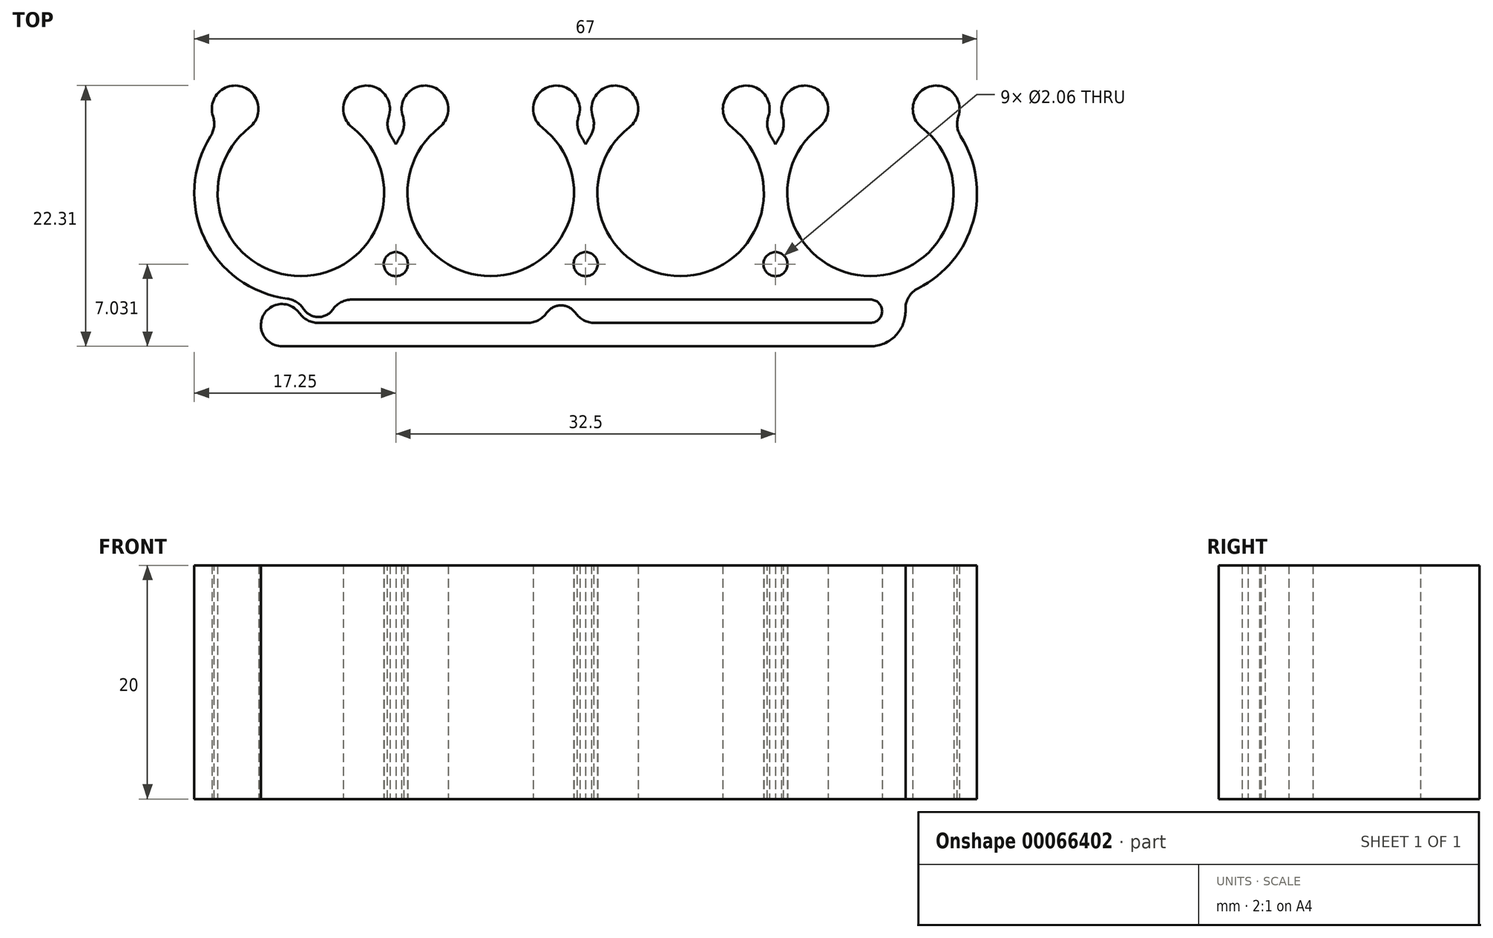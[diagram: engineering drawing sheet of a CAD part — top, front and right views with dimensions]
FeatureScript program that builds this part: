
annotation { "Feature Type Name" : "Feature", "Feature Type Description" : "" }
export const myFeature = defineFeature(function(context is Context, id is Id, definition is map)
    precondition{}
    {
        {
            assignVariable(context, id + "F0", {"name" : "Wall", "anyValue" : 2});
        }
        {
            var Q0;
            Q0=qCreatedBy(makeId("Top.planeOp"),FACE);
            var sketch = newSketch(context, id + "F1", { "sketchPlane" : qUnion([Q0])});
            skCircle(sketch, "E0", {"center": v(-24.38, 9.13) * mm, "radius": 7.12 * mm});
            skCircle(sketch, "E1", {"center": v(-8.12, 9.13) * mm, "radius": 7.12 * mm});
            skCircle(sketch, "E2", {"center": v(8.12, 9.13) * mm, "radius": 7.12 * mm});
            skCircle(sketch, "E3", {"center": v(24.38, 9.12) * mm, "radius": 7.12 * mm});
            skLineSegment(sketch, "E4", {"start": v(-24.37, 0) * mm, "end": v(24.37, 0) * mm});
            skArc(sketch, "E5", {"start": v(-31.43, 14.91) * mm, "mid": v(-32.62, 5.22) * mm, "end": v(-24.38, 0) * mm});
            skArc(sketch, "E6", {"start": v(-16.25, 13.28) * mm, "mid": v(-16.74, 14.12) * mm, "end": v(-17.32, 14.91) * mm});
            skArc(sketch, "E7", {"start": v(-15.18, 14.91) * mm, "mid": v(-15.76, 14.12) * mm, "end": v(-16.25, 13.28) * mm});
            skArc(sketch, "E8", {"start": v(-28.77, 14.74) * mm, "mid": v(-29.87, 18.3) * mm, "end": v(-31.43, 14.91) * mm});
            skArc(sketch, "E9", {"start": v(-17.32, 14.91) * mm, "mid": v(-18.88, 18.3) * mm, "end": v(-19.98, 14.74) * mm});
            skArc(sketch, "E10", {"start": v(-12.52, 14.74) * mm, "mid": v(-13.62, 18.3) * mm, "end": v(-15.18, 14.91) * mm});
            skCircle(sketch, "E11", {"center": v(-16.25, 3.03) * mm, "radius": 1.03 * mm});
            skCircle(sketch, "E12", {"center": v(0, 3.03) * mm, "radius": 1.03 * mm});
            skArc(sketch, "E13", {"start": v(0, 13.28) * mm, "mid": v(-0.5, 14.12) * mm, "end": v(-1.07, 14.91) * mm});
            skArc(sketch, "E14", {"start": v(-1.07, 14.91) * mm, "mid": v(-2.63, 18.3) * mm, "end": v(-3.73, 14.74) * mm});
            skArc(sketch, "E15.MirrorCS", {"start": v(0, 13.28) * mm, "mid": v(0.5, 14.12) * mm, "end": v(1.07, 14.91) * mm});
            skArc(sketch, "E16.MirrorCS", {"start": v(1.07, 14.91) * mm, "mid": v(2.63, 18.3) * mm, "end": v(3.73, 14.74) * mm});
            skArc(sketch, "E17.MirrorCS", {"start": v(12.52, 14.74) * mm, "mid": v(13.62, 18.3) * mm, "end": v(15.18, 14.91) * mm});
            skArc(sketch, "E18.MirrorCS", {"start": v(15.18, 14.91) * mm, "mid": v(15.76, 14.12) * mm, "end": v(16.25, 13.28) * mm});
            skArc(sketch, "E19.MirrorCS", {"start": v(16.25, 13.28) * mm, "mid": v(16.74, 14.12) * mm, "end": v(17.32, 14.91) * mm});
            skArc(sketch, "E20.MirrorCS", {"start": v(17.32, 14.91) * mm, "mid": v(18.88, 18.3) * mm, "end": v(19.98, 14.74) * mm});
            skArc(sketch, "E21.MirrorCS", {"start": v(28.77, 14.74) * mm, "mid": v(29.87, 18.3) * mm, "end": v(31.43, 14.91) * mm});
            skArc(sketch, "E22.MirrorCS", {"start": v(31.43, 14.91) * mm, "mid": v(32.62, 5.22) * mm, "end": v(24.38, 0) * mm});
            skCircle(sketch, "E23.MirrorC", {"center": v(16.25, 3.03) * mm, "radius": 1.03 * mm});
            skLineSegment(sketch, "E24", {"start": v(-24.2, -2) * mm, "end": v(24.38, -2) * mm});
            skArc(sketch, "E25", {"start": v(24.38, -2) * mm, "mid": v(25.38, -1) * mm, "end": v(24.38, 0) * mm});
            skLineSegment(sketch, "E26", {"start": v(-25.99, -4) * mm, "end": v(24.38, -4) * mm});
            skArc(sketch, "E27", {"start": v(24.38, -4) * mm, "mid": v(26.94, -2.55) * mm, "end": v(27.03, 0.4) * mm});
            skArc(sketch, "E28", {"start": v(-24.38, 0) * mm, "mid": v(-22.88, -1.5) * mm, "end": v(-21.38, 0) * mm});
            skArc(sketch, "E29", {"start": v(-24.2, -2) * mm, "mid": v(-27.33, -0.99) * mm, "end": v(-25.99, -4) * mm});
            skArc(sketch, "E30", {"start": v(-0.6, -2) * mm, "mid": v(-2.1, -0.5) * mm, "end": v(-3.6, -2) * mm});
            skSolve(sketch);
        }
        {
            var Q0;
            Q0=makeQuery(id+"F1.imprint","IMPRINT",FACE,{"disambiguationData":[TD([[makeQuery(id+"F1.imprint","IMPRINT",EDGE,{"derivedFrom":sQuery(id+"F1.wireOp",EDGE,"E4")}),1.0]])]});
            var Q1;
            Q1=makeQuery(id+"F1.imprint","IMPRINT",FACE,{"disambiguationData":[TD([[makeQuery(id+"F1.imprint","IMPRINT",EDGE,{"derivedFrom":sQuery(id+"F1.wireOp",EDGE,"E24")}),-1.0]])]});
            var Q2;
            {var subQ0=sQuery(id+"F1.wireOp",EDGE,"E28");Q2=makeQuery(id+"F1.imprint","IMPRINT",FACE,{"disambiguationData":[TD([[makeQuery(id+"F1.imprint","IMPRINT",EDGE,{"derivedFrom":subQ0}),1.0]])]});}
            var Q3;
            {var subQ0=sQuery(id+"F1.wireOp",EDGE,"E30");Q3=makeQuery(id+"F1.imprint","IMPRINT",FACE,{"disambiguationData":[TD([[makeQuery(id+"F1.imprint","IMPRINT",EDGE,{"derivedFrom":subQ0}),1.0]])]});}
            extrude(context, id + "F2", {"entities" : qUnion([Q0, Q1, Q2, Q3]), "endBound" : BoundingType.SYMMETRIC, "depth" : 20 * mm});
        }
        {
            var Q0;
            Q0=makeQuery(id+"F2.opExtrude","SWEPT_EDGE",EDGE,{"disambiguationData":[OSD([sQuery(id+"F1.wireOp",EDGE,"E21.MirrorCS"),sQuery(id+"F1.wireOp",EDGE,"E22.MirrorCS")])]});
            var Q1;
            Q1=makeQuery(id+"F2.opExtrude","SWEPT_EDGE",EDGE,{"disambiguationData":[OSD([sQuery(id+"F1.wireOp",EDGE,"E17.MirrorCS"),sQuery(id+"F1.wireOp",EDGE,"E18.MirrorCS")])]});
            var Q2;
            Q2=makeQuery(id+"F2.opExtrude","SWEPT_EDGE",EDGE,{"disambiguationData":[OSD([sQuery(id+"F1.wireOp",EDGE,"E19.MirrorCS"),sQuery(id+"F1.wireOp",EDGE,"E20.MirrorCS")])]});
            var Q3;
            Q3=makeQuery(id+"F2.opExtrude","SWEPT_EDGE",EDGE,{"disambiguationData":[OSD([sQuery(id+"F1.wireOp",EDGE,"E15.MirrorCS"),sQuery(id+"F1.wireOp",EDGE,"E16.MirrorCS")])]});
            var Q4;
            Q4=makeQuery(id+"F2.opExtrude","SWEPT_EDGE",EDGE,{"disambiguationData":[OSD([sQuery(id+"F1.wireOp",EDGE,"E7"),sQuery(id+"F1.wireOp",EDGE,"E10")])]});
            var Q5;
            Q5=makeQuery(id+"F2.opExtrude","SWEPT_EDGE",EDGE,{"disambiguationData":[OSD([sQuery(id+"F1.wireOp",EDGE,"E5"),sQuery(id+"F1.wireOp",EDGE,"E8")])]});
            var Q6;
            Q6=makeQuery(id+"F2.opExtrude","SWEPT_EDGE",EDGE,{"disambiguationData":[OSD([sQuery(id+"F1.wireOp",EDGE,"E6"),sQuery(id+"F1.wireOp",EDGE,"E9")])]});
            var Q7;
            Q7=makeQuery(id+"F2.opExtrude","SWEPT_EDGE",EDGE,{"disambiguationData":[OSD([sQuery(id+"F1.wireOp",EDGE,"E13"),sQuery(id+"F1.wireOp",EDGE,"E14")])]});
            var Q8;
            Q8=makeQuery(id+"F2.opExtrude","SWEPT_EDGE",EDGE,{"disambiguationData":[OSD([sQuery(id+"F1.wireOp",EDGE,"E4"),sQuery(id+"F1.wireOp",EDGE,"E28")])]});
            var Q9;
            Q9=makeQuery(id+"F2.opExtrude","SWEPT_EDGE",EDGE,{"disambiguationData":[OSD([sQuery(id+"F1.wireOp",EDGE,"E22.MirrorCS"),sQuery(id+"F1.wireOp",EDGE,"E27")])]});
            var Q10;
            Q10=makeQuery(id+"F2.opExtrude","SWEPT_EDGE",EDGE,{"disambiguationData":[OSD([sQuery(id+"F1.wireOp",EDGE,"E4"),sQuery(id+"F1.wireOp",EDGE,"E5"),sQuery(id+"F1.wireOp",EDGE,"E28")])]});
            var Q11;
            Q11=makeQuery(id+"F2.opExtrude","SWEPT_EDGE",EDGE,{"disambiguationData":[OSD([sQuery(id+"F1.wireOp",EDGE,"E24"),sQuery(id+"F1.wireOp",EDGE,"E29")])]});
            var Q12;
            {var subQ0=sQuery(id+"F1.wireOp",EDGE,"E30");var subQ1=sQuery(id+"F1.wireOp",EDGE,"E24");Q12=makeQuery(id+"F2.opExtrude","SWEPT_EDGE",EDGE,{"disambiguationData":[OSD([subQ1,subQ0]),TDD([makeQuery(id+"F1.imprint","INTERSECT",VERTEX,{"disambiguationData":[OD(0.0)],"derivedFrom":[subQ1,subQ0]})])]});}
            var Q13;
            {var subQ0=sQuery(id+"F1.wireOp",EDGE,"E30");var subQ1=sQuery(id+"F1.wireOp",EDGE,"E24");Q13=makeQuery(id+"F2.opExtrude","SWEPT_EDGE",EDGE,{"disambiguationData":[OSD([subQ1,subQ0]),TDD([makeQuery(id+"F1.imprint","INTERSECT",VERTEX,{"disambiguationData":[OD(1.0)],"derivedFrom":[subQ1,subQ0]})])]});}
            fillet(context, id + "F3", {"entities" : qUnion([Q0, Q1, Q2, Q3, Q4, Q5, Q6, Q7, Q8, Q9, Q10, Q11, Q12, Q13]), "radius" : (getVariable(context, 'Wall')) * mm, "tangentPropagation" : true, "allowEdgeOverflow" : false});
        }
    });
